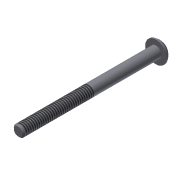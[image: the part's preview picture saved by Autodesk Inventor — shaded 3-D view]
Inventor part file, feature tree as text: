
AUTODESK INVENTOR PART (.ipt)
format: ipt  version: 2013 (Build 170138000, 138)  size: 106,496 bytes
history: native  units: in
note: dims shown in document units (in); Inventor stores cm internally (conversion verified against a paired STEP export)
features: sketch x3, extrude x2, revolve x1, chamfer x1, thread x1
ambient origin geometry x8: Origin, YZ Plane, XZ Plane, XY Plane, X Axis, Y Axis, Z Axis, Center Point
bodies: Solid1 (feature_tree)
feature tree (8):
  extrude  "Extrusion1"  Depth=2.0in TaperAngle=0.0deg
  revolve  "Revolution1"  [1 undecoded]
  extrude  "Extrusion2"  Depth=0.0938in
  chamfer  "Chamfer1"  Distance=0.0625in
  thread  "Thread1"  [1 undecoded]
  sketch  "Sketch1"  dims[d0=0.164in d1=2.0in d2=0.0in]
  sketch  "Sketch2"  dims[d3=0.087in d6=0.08in]
  sketch  "Sketch3"  dims[d7=90.0deg d8=0.0938in d9=0.0625in d10=0.0in d13=0.02in d14=0.125in d15=45.0deg d16=1.0in d17=0.0in d19=0.156in]
note: 2 required parameter values undecoded (feature->parameter linkage not recoverable at this tier; creation-order binding heuristic only, values carry confidence <= 0.55)